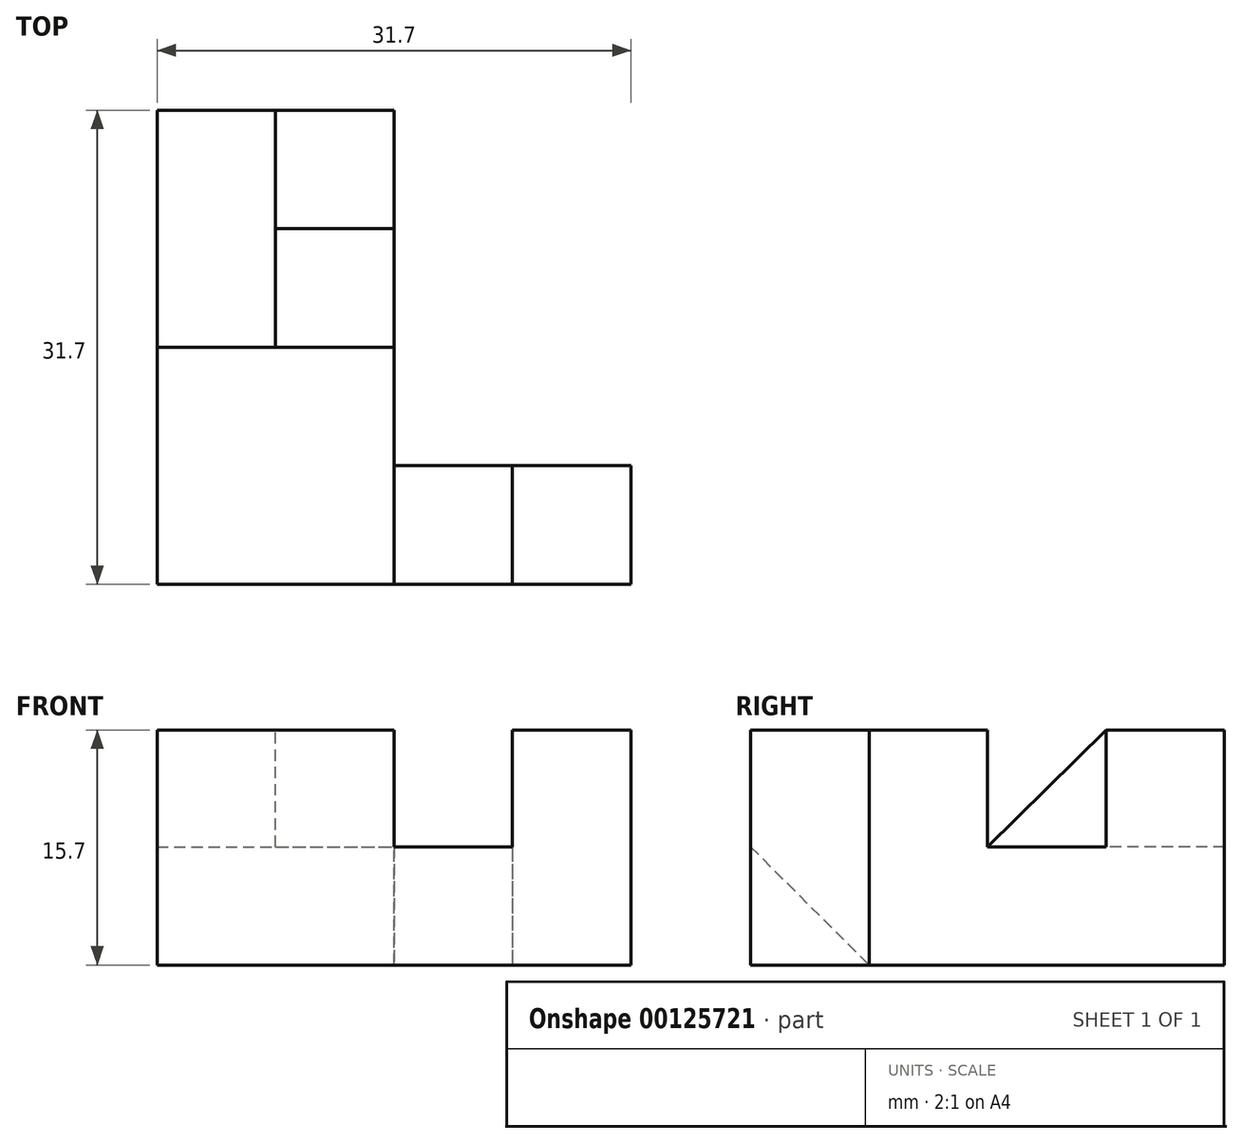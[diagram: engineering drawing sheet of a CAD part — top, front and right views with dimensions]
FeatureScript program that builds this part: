
annotation { "Feature Type Name" : "Feature", "Feature Type Description" : "" }
export const myFeature = defineFeature(function(context is Context, id is Id, definition is map)
    precondition{}
    {
        {
            var Q0;
            Q0=qCreatedBy(makeId("Top.planeOp"),FACE);
            var sketch = newSketch(context, id + "F0", { "sketchPlane" : qUnion([Q0])});
            skLineSegment(sketch, "E0", {"start": v(0, 0) * mm, "end": v(0, -31.7) * mm});
            skLineSegment(sketch, "E1", {"start": v(0, 0) * mm, "end": v(31.7, 0) * mm});
            skLineSegment(sketch, "E2", {"start": v(31.7, 0) * mm, "end": v(31.7, -31.7) * mm});
            skLineSegment(sketch, "E3", {"start": v(0, -31.7) * mm, "end": v(31.7, -31.7) * mm});
            skSolve(sketch);
        }
        {
            var Q0;
            Q0 = qSketchRegion(id + "F0", true);
            extrude(context, id + "F1", {"entities" : qUnion([Q0]), "depth" : 7.9 * mm});
        }
        {
            var Q0;
            Q0=makeQuery(id+"F1.opExtrude","CAP_FACE",FACE,{"disambiguationData":[OSD([sQuery(id+"F0.wireOp",EDGE,"E0"),sQuery(id+"F0.wireOp",EDGE,"E1"),sQuery(id+"F0.wireOp",EDGE,"E2"),sQuery(id+"F0.wireOp",EDGE,"E3")])],"isStart":false});
            var sketch = newSketch(context, id + "F2", { "sketchPlane" : qUnion([Q0])});
            skLineSegment(sketch, "E4", {"start": v(15.85, -15.85) * mm, "end": v(15.85, -31.7) * mm});
            skLineSegment(sketch, "E5", {"start": v(0, -15.85) * mm, "end": v(15.85, -15.85) * mm});
            skSolve(sketch);
        }
        {
            var Q0;
            Q0 = qSketchRegion(id + "F2", true);
            var Q1;
            {var subQ0=sQuery(id+"F2.wireOp",EDGE,"E4");Q1=makeQuery(id+"F2.imprint","IMPRINT",FACE,{"disambiguationData":[TD([[makeQuery(id+"F2.imprint","IMPRINT",EDGE,{"derivedFrom":subQ0}),-1.0]])]});}
            extrude(context, id + "F3", {"entities" : qUnion([Q0, Q1]), "operationType" : NewBodyOperationType.ADD, "depth" : 7.8 * mm});
        }
        {
            var Q0;
            Q0=makeQuery(id+"F1.opExtrude","CAP_FACE",FACE,{"disambiguationData":[OSD([sQuery(id+"F0.wireOp",EDGE,"E0"),sQuery(id+"F0.wireOp",EDGE,"E1"),sQuery(id+"F0.wireOp",EDGE,"E2"),sQuery(id+"F0.wireOp",EDGE,"E3")])],"isStart":false});
            var sketch = newSketch(context, id + "F4", { "sketchPlane" : qUnion([Q0])});
            skLineSegment(sketch, "E6", {"start": v(0, -15.85) * mm, "end": v(0, 0) * mm});
            skLineSegment(sketch, "E7", {"start": v(0, 0) * mm, "end": v(15.85, 0) * mm});
            skLineSegment(sketch, "E8", {"start": v(15.85, 0) * mm, "end": v(15.85, -15.85) * mm});
            skLineSegment(sketch, "E9", {"start": v(15.85, -23.77) * mm, "end": v(31.7, -23.77) * mm});
            skLineSegment(sketch, "E10", {"start": v(31.7, -23.77) * mm, "end": v(31.7, -31.7) * mm});
            skLineSegment(sketch, "E11", {"start": v(31.7, -31.7) * mm, "end": v(15.85, -31.7) * mm});
            skLineSegment(sketch, "E12", {"start": v(15.85, -31.7) * mm, "end": v(15.85, -23.77) * mm});
            skSolve(sketch);
        }
        {
            var Q0;
            {var subQ4=sQuery(id+"F4.wireOp",EDGE,"E8");Q0=makeQuery(id+"F4.imprint","IMPRINT",FACE,{"disambiguationData":[TD([[makeQuery(id+"F4.imprint","IMPRINT",EDGE,{"derivedFrom":subQ4}),1.0]])]});}
            extrude(context, id + "F5", {"entities" : qUnion([Q0]), "operationType" : NewBodyOperationType.REMOVE, "oppositeDirection" : true, "depth" : 25 * mm});
        }
        {
            var Q0;
            {var subQ1=sQuery(id+"F0.wireOp",EDGE,"E3");var subQ2=sQuery(id+"F0.wireOp",EDGE,"E2");Q0=makeQuery(id+"F5.boolean.opBoolean","SPLIT",FACE,{"disambiguationData":[TD([makeQuery(id+"F1.opExtrude","SWEPT_FACE",FACE,{"disambiguationData":[OSD([subQ2])]})])],"derivedFrom":makeQuery(id+"F1.opExtrude","CAP_FACE",FACE,{"disambiguationData":[OSD([sQuery(id+"F0.wireOp",EDGE,"E0"),sQuery(id+"F0.wireOp",EDGE,"E1"),subQ2,subQ1])],"isStart":false})});}
            var sketch = newSketch(context, id + "F6", { "sketchPlane" : qUnion([Q0])});
            skLineSegment(sketch, "E13", {"start": v(23.77, -23.77) * mm, "end": v(23.77, -31.7) * mm});
            skLineSegment(sketch, "E14", {"start": v(23.77, -31.7) * mm, "end": v(31.7, -31.7) * mm});
            skLineSegment(sketch, "E15", {"start": v(31.7, -31.7) * mm, "end": v(31.7, -23.77) * mm});
            skLineSegment(sketch, "E16", {"start": v(31.7, -23.77) * mm, "end": v(23.77, -23.77) * mm});
            skSolve(sketch);
        }
        {
            var Q0;
            Q0=makeQuery(id+"F6.imprint","IMPRINT",FACE,{"disambiguationData":[TD([[makeQuery(id+"F6.imprint","IMPRINT",EDGE,{"derivedFrom":sQuery(id+"F6.wireOp",EDGE,"E13")}),1.0]])]});
            extrude(context, id + "F7", {"entities" : qUnion([Q0]), "operationType" : NewBodyOperationType.ADD, "depth" : 7.8 * mm});
        }
        {
            var Q0;
            {var subQ0=sQuery(id+"F0.wireOp",EDGE,"E1");var subQ2=sQuery(id+"F0.wireOp",EDGE,"E0");Q0=makeQuery(id+"F5.boolean.opBoolean","SPLIT",FACE,{"disambiguationData":[TD([makeQuery(id+"F1.opExtrude","SWEPT_FACE",FACE,{"disambiguationData":[OSD([subQ2])]})])],"derivedFrom":makeQuery(id+"F1.opExtrude","CAP_FACE",FACE,{"disambiguationData":[OSD([subQ2,subQ0,sQuery(id+"F0.wireOp",EDGE,"E2"),sQuery(id+"F0.wireOp",EDGE,"E3")])],"isStart":false})});}
            var sketch = newSketch(context, id + "F8", { "sketchPlane" : qUnion([Q0])});
            skLineSegment(sketch, "E17", {"start": v(7.92, 0) * mm, "end": v(7.92, -7.92) * mm});
            skPoint(sketch, "E17.endSnap0", {"position": v(15.85, -7.92) * mm});
            skLineSegment(sketch, "E18", {"start": v(7.92, -7.92) * mm, "end": v(15.85, -7.92) * mm});
            skLineSegment(sketch, "E19", {"start": v(15.85, 0) * mm, "end": v(7.92, 0) * mm});
            skSolve(sketch);
        }
        {
            var Q0;
            Q0=makeQuery(id+"F8.imprint","IMPRINT",FACE,{"disambiguationData":[TD([[makeQuery(id+"F8.imprint","IMPRINT",EDGE,{"derivedFrom":sQuery(id+"F8.wireOp",EDGE,"E17")}),1.0]])]});
            extrude(context, id + "F9", {"entities" : qUnion([Q0]), "operationType" : NewBodyOperationType.ADD, "depth" : 7.8 * mm});
        }
        {
            var Q0;
            {var subQ0=sQuery(id+"F4.wireOp",EDGE,"E8");var subQ1=sQuery(id+"F2.wireOp",EDGE,"E4");Q0=makeQuery(id+"F9.boolean.opBoolean","MERGE",FACE,{"derivedFrom":[makeQuery(id+"F5.boolean.opBoolean","MERGE",FACE,{"derivedFrom":[makeQuery(id+"F3.opExtrude","SWEPT_FACE",FACE,{"disambiguationData":[OSD([subQ1])]}),makeQuery(id+"F5.opExtrude","SWEPT_FACE",FACE,{"disambiguationData":[OSD([subQ1,subQ0])]})]}),makeQuery(id+"F9.opExtrude","SWEPT_FACE",FACE,{"disambiguationData":[OSD([subQ1,subQ0])]})]});}
            var sketch = newSketch(context, id + "F10", { "sketchPlane" : qUnion([Q0])});
            skLineSegment(sketch, "E20", {"start": v(-7.92, 15.7) * mm, "end": v(-15.85, 7.9) * mm});
            skSolve(sketch);
        }
        {
            var Q0;
            Q0 = qSketchRegion(id + "F10", true);
            var Q1;
            Q1=makeQuery(id+"F10.imprint","IMPRINT",FACE,{"disambiguationData":[TD([[makeQuery(id+"F10.imprint","IMPRINT",EDGE,{"derivedFrom":sQuery(id+"F10.wireOp",EDGE,"E20")}),1.0]])]});
            var Q2;
            Q2=makeQuery(id+"F9.opExtrude","SWEPT_FACE",FACE,{"disambiguationData":[OSD([sQuery(id+"F8.wireOp",EDGE,"E17")])]});
            extrude(context, id + "F11", {"entities" : qUnion([Q0, Q1]), "endBound" : BoundingType.UP_TO_SURFACE, "oppositeDirection" : true, "endBoundEntityFace" : qUnion([Q2]), "depth" : 25 * mm});
        }
        {
            var Q0;
            {var subQ0=sQuery(id+"F4.wireOp",EDGE,"E8");var subQ1=sQuery(id+"F2.wireOp",EDGE,"E4");Q0=makeQuery(id+"F9.boolean.opBoolean","MERGE",FACE,{"derivedFrom":[makeQuery(id+"F5.boolean.opBoolean","MERGE",FACE,{"derivedFrom":[makeQuery(id+"F3.opExtrude","SWEPT_FACE",FACE,{"disambiguationData":[OSD([subQ1])]}),makeQuery(id+"F5.opExtrude","SWEPT_FACE",FACE,{"disambiguationData":[OSD([subQ1,subQ0])]})]}),makeQuery(id+"F9.opExtrude","SWEPT_FACE",FACE,{"disambiguationData":[OSD([subQ1,subQ0])]})]});}
            var sketch = newSketch(context, id + "F12", { "sketchPlane" : qUnion([Q0])});
            skLineSegment(sketch, "E21", {"start": v(-31.7, 7.9) * mm, "end": v(-23.77, 0) * mm});
            skLineSegment(sketch, "E22", {"start": v(-23.77, 0) * mm, "end": v(-23.77, 7.9) * mm});
            skLineSegment(sketch, "E23", {"start": v(-23.77, 7.9) * mm, "end": v(-31.7, 7.9) * mm});
            skSolve(sketch);
        }
        {
            var Q0;
            Q0 = qSketchRegion(id + "F12", true);
            var Q1;
            Q1=makeQuery(id+"F7.opExtrude","SWEPT_FACE",FACE,{"disambiguationData":[OSD([sQuery(id+"F6.wireOp",EDGE,"E13")])]});
            extrude(context, id + "F13", {"entities" : qUnion([Q0]), "operationType" : NewBodyOperationType.REMOVE, "endBound" : BoundingType.UP_TO_SURFACE, "endBoundEntityFace" : qUnion([Q1]), "depth" : 25 * mm});
        }
    });
